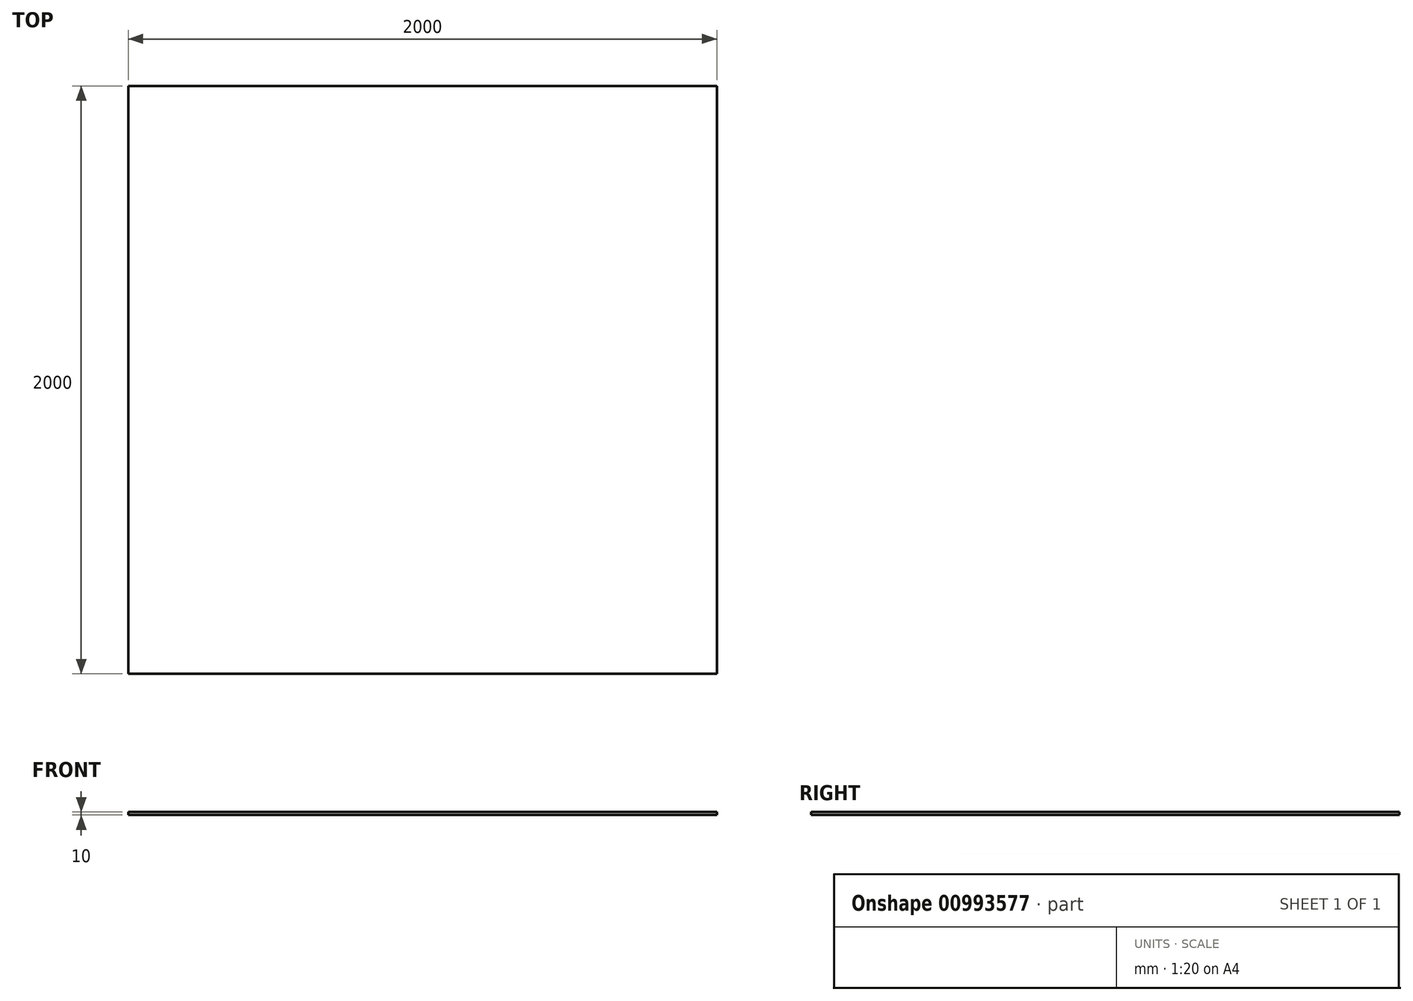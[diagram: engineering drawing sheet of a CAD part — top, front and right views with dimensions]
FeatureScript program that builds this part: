
annotation { "Feature Type Name" : "Feature", "Feature Type Description" : "" }
export const myFeature = defineFeature(function(context is Context, id is Id, definition is map)
    precondition{}
    {
        {
            var Q0;
            Q0=qCreatedBy(makeId("Top.planeOp"),FACE);
            var sketch = newSketch(context, id + "F0", { "sketchPlane" : qUnion([Q0])});
            skLineSegment(sketch, "E0.bottom", {"start": v(1000, 1000) * mm, "end": v(-1000, 1000) * mm});
            skLineSegment(sketch, "E0.top", {"start": v(1000, -1000) * mm, "end": v(-1000, -1000) * mm});
            skLineSegment(sketch, "E0.left", {"start": v(1000, 1000) * mm, "end": v(1000, -1000) * mm});
            skLineSegment(sketch, "E0.right", {"start": v(-1000, 1000) * mm, "end": v(-1000, -1000) * mm});
            skPoint(sketch, "E0.middle", {"position": v(0, 0) * mm});
            skSolve(sketch);
        }
        {
            var Q0;
            Q0 = qSketchRegion(id + "F0", true);
            extrude(context, id + "F1", {"entities" : qUnion([Q0]), "depth" : 10 * mm, "offsetDistance" : 25 * mm});
        }
    });
